# Revit family: 63_UN_FreeStanding_SPF MAXI_Norton
name_source: partatom
category: Lighting Fixtures
units: mm (PartAtom-declared; Revit-internal decimal feet)

## family parameters
Always vertical = Yes
Cut with Voids When Loaded = Yes
Light Source = No
OmniClass Number = 23.80.70.11.14.11
OmniClass Title = Downlights
Part Type = Normal
Room Calculation Point = Yes
Round Connector Dimension = Use Diameter
Shared = No
Work Plane-Based = No

## types (2) — shared parameters
Apparent Load = 70 VA
Assembly Code = 63.0
Calc_Symbol_Length = 393 mm  [stored 1.28937 ft]
Calc_Symbol_Width = 240 mm  [stored 0.787402 ft]
Description = IP66 / IK10
Housing_Material = Anthracite
IfcExportAs = IfcLightFixtureType
IfcExportType = USERDEFINED
Lamp = LED
Luminous Flux (lm) = 8759 lm
Manufacturer = Norton
Model = SPF
URL = https://www.norton.nl
Voltage = 230 V
Wattage Comments = 70W
Weight = 2,5kg

## per-type parameters (varying)
| type | Light Source |
| SPFMAXI83LM8800 | SPF_MIDI Geometry : SPFMAXI83LM8800 |
| SPFMAXI84LM8800 | SPF_MIDI Geometry : SPFMAXI84LM8800 |

note: [stored X ft] marks values corroborated as IEEE doubles in the binary element streams (Revit-internal decimal feet)

## geometry (parser evidence)
native form markers: Sweep x13
no freeform markers — native parametric forms only
